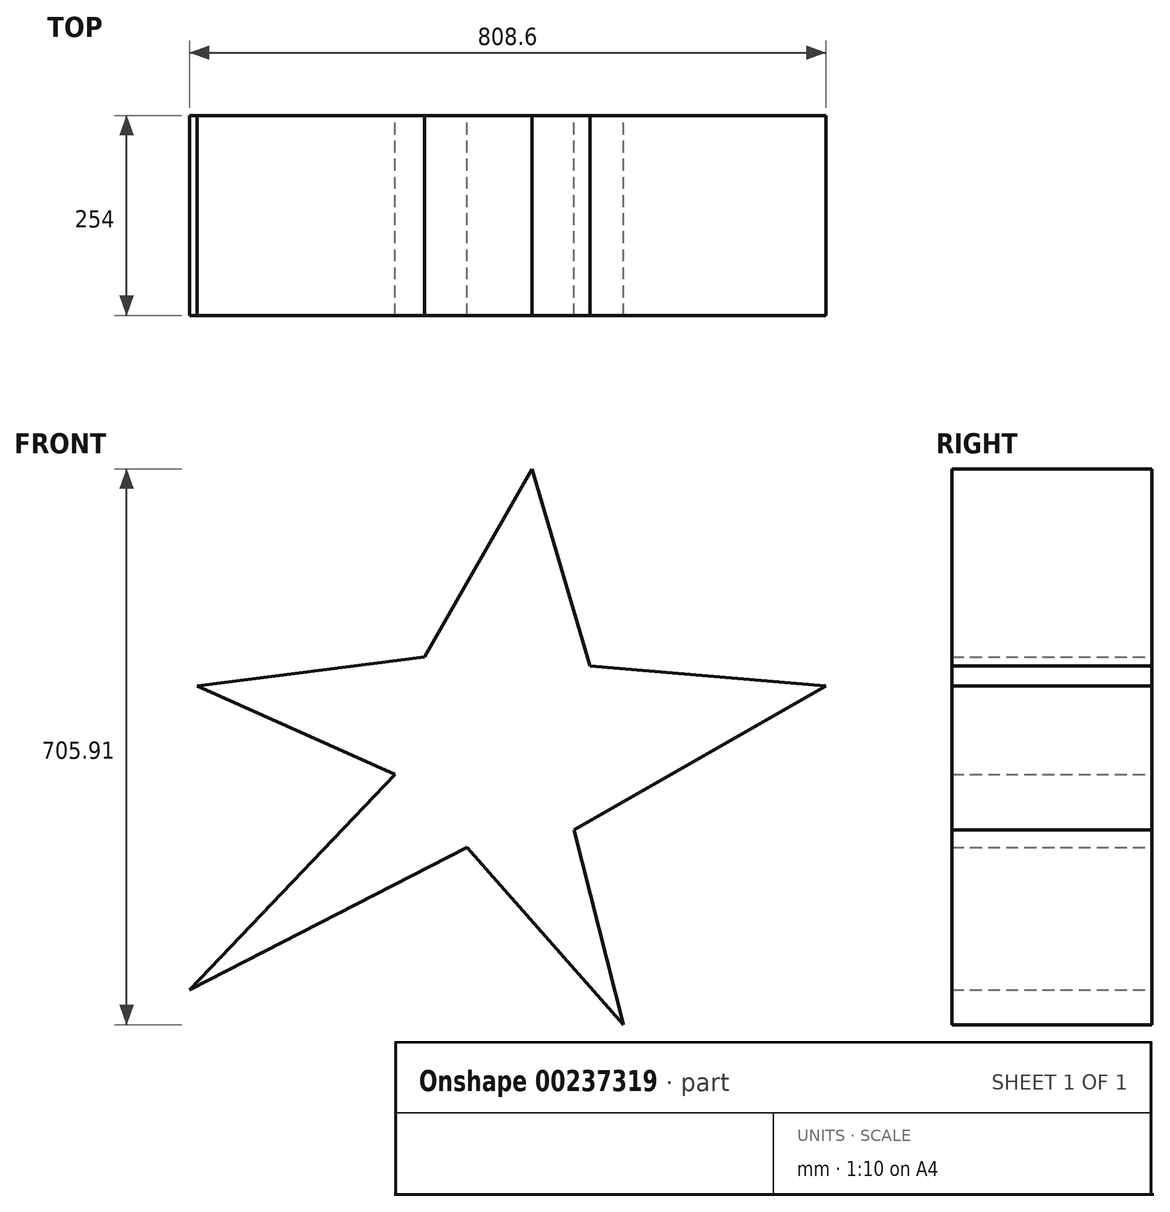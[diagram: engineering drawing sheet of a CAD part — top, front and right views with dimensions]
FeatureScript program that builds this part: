
annotation { "Feature Type Name" : "Feature", "Feature Type Description" : "" }
export const myFeature = defineFeature(function(context is Context, id is Id, definition is map)
    precondition{}
    {
        {
            var Q0;
            Q0=qCreatedBy(makeId("Front.planeOp"),FACE);
            var sketch = newSketch(context, id + "F0", { "sketchPlane" : qUnion([Q0])});
            skCircle(sketch, "E0", {"center": v(-62.47, 44.6) * mm, "radius": 144.43 * mm});
            skLineSegment(sketch, "E1", {"start": v(-162.18, 149.1) * mm, "end": v(-26.06, 388.13) * mm});
            skLineSegment(sketch, "E2", {"start": v(-26.06, 388.13) * mm, "end": v(47.64, 138.07) * mm});
            skLineSegment(sketch, "E3", {"start": v(47.64, 138.07) * mm, "end": v(347.51, 112.8) * mm});
            skLineSegment(sketch, "E4", {"start": v(347.51, 112.8) * mm, "end": v(27.5, -70.3) * mm});
            skLineSegment(sketch, "E5", {"start": v(27.5, -70.3) * mm, "end": v(90.14, -317.78) * mm});
            skLineSegment(sketch, "E6", {"start": v(90.14, -317.78) * mm, "end": v(-108.24, -92.38) * mm});
            skLineSegment(sketch, "E7", {"start": v(-108.24, -92.38) * mm, "end": v(-461.09, -273.32) * mm});
            skLineSegment(sketch, "E8", {"start": v(-461.09, -273.32) * mm, "end": v(-199.84, 0) * mm});
            skLineSegment(sketch, "E9", {"start": v(-199.84, 0) * mm, "end": v(-451.49, 112.8) * mm});
            skLineSegment(sketch, "E10", {"start": v(-451.49, 112.8) * mm, "end": v(-162.18, 149.1) * mm});
            skSolve(sketch);
        }
        {
            var Q0;
            {var subQ0=sQuery(id+"F0.wireOp",EDGE,"E1");Q0=makeQuery(id+"F0.imprint","IMPRINT",FACE,{"disambiguationData":[TD([[makeQuery(id+"F0.imprint","IMPRINT",EDGE,{"derivedFrom":subQ0}),-1.0]])]});}
            var Q1;
            {var subQ0=sQuery(id+"F0.wireOp",EDGE,"E7");Q1=makeQuery(id+"F0.imprint","IMPRINT",FACE,{"disambiguationData":[TD([[makeQuery(id+"F0.imprint","IMPRINT",EDGE,{"derivedFrom":subQ0}),-1.0]])]});}
            var Q2;
            {var subQ0=sQuery(id+"F0.wireOp",EDGE,"E3");Q2=makeQuery(id+"F0.imprint","IMPRINT",FACE,{"disambiguationData":[TD([[makeQuery(id+"F0.imprint","IMPRINT",EDGE,{"derivedFrom":subQ0}),-1.0]])]});}
            var Q3;
            {var subQ0=sQuery(id+"F0.wireOp",EDGE,"E0");var subQ1=makeQuery(id+"F0.imprint","INTERSECT",VERTEX,{"derivedFrom":[subQ0,sQuery(id+"F0.wireOp",EDGE,"E1"),sQuery(id+"F0.wireOp",EDGE,"E10")]});Q3=makeQuery(id+"F0.imprint","IMPRINT",FACE,{"disambiguationData":[TD([[makeQuery(id+"F0.imprint","IMPRINT",EDGE,{"disambiguationData":[TD([[subQ1,1.0]])],"derivedFrom":subQ0}),1.0]])]});}
            var Q4;
            {var subQ2=sQuery(id+"F0.wireOp",EDGE,"E9");Q4=makeQuery(id+"F0.imprint","IMPRINT",FACE,{"disambiguationData":[TD([[makeQuery(id+"F0.imprint","IMPRINT",EDGE,{"derivedFrom":subQ2}),-1.0]])]});}
            extrude(context, id + "F1", {"entities" : qUnion([Q0, Q1, Q2, Q3, Q4]), "depth" : 254 * mm});
        }
    });
